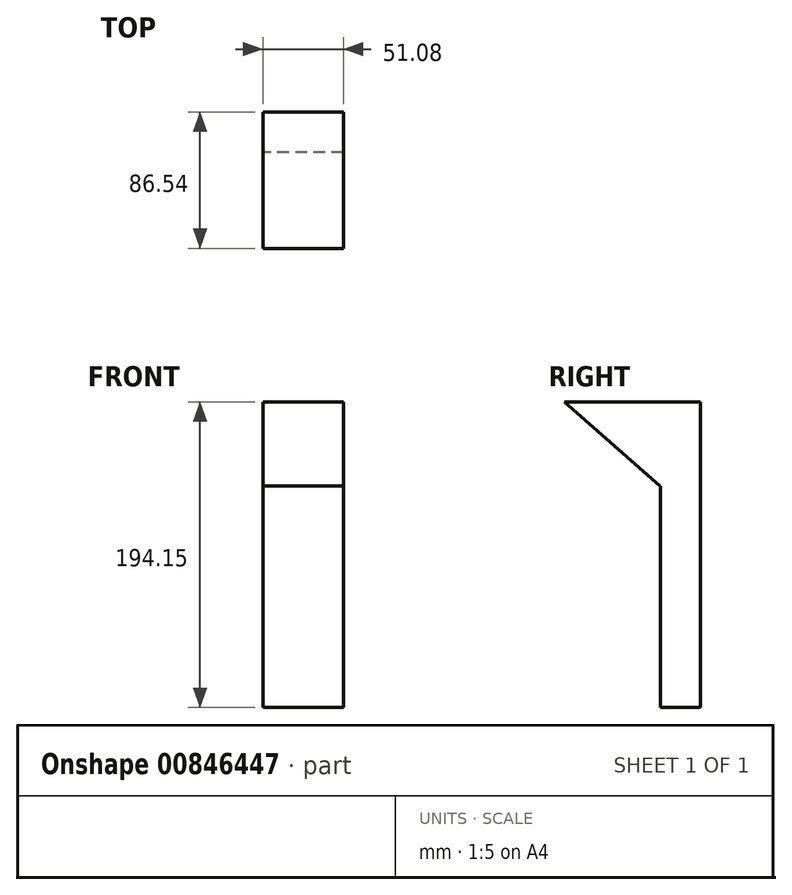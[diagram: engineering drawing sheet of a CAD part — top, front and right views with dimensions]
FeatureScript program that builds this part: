
annotation { "Feature Type Name" : "Feature", "Feature Type Description" : "" }
export const myFeature = defineFeature(function(context is Context, id is Id, definition is map)
    precondition{}
    {
        {
            var Q0;
            Q0=qCreatedBy(makeId("Front.planeOp"),FACE);
            var sketch = newSketch(context, id + "F0", { "sketchPlane" : qUnion([Q0])});
            skLineSegment(sketch, "E0.bottom", {"start": v(-51.08, -57.08) * mm, "end": v(0, -57.08) * mm});
            skLineSegment(sketch, "E0.top", {"start": v(-51.08, 60.33) * mm, "end": v(0, 60.33) * mm});
            skLineSegment(sketch, "E0.left", {"start": v(-51.08, -57.08) * mm, "end": v(-51.08, 60.33) * mm});
            skLineSegment(sketch, "E0.right", {"start": v(0, -57.08) * mm, "end": v(0, 60.33) * mm});
            skSolve(sketch);
        }
        {
            var Q0;
            Q0=makeQuery(id+"F0.imprint","IMPRINT",FACE,{"disambiguationData":[TD([[makeQuery(id+"F0.imprint","IMPRINT",EDGE,{"derivedFrom":sQuery(id+"F0.wireOp",EDGE,"E0.bottom")}),1.0]])]});
            extrude(context, id + "F1", {"entities" : qUnion([Q0]), "depth" : 25.4 * mm, "offsetDistance" : 25.4 * mm});
        }
        {
            var Q0;
            Q0=makeQuery(id+"F1.opExtrude","SWEPT_FACE",FACE,{"disambiguationData":[OSD([sQuery(id+"F0.wireOp",EDGE,"E0.top")])]});
            extrude(context, id + "F2", {"entities" : qUnion([Q0]), "operationType" : NewBodyOperationType.ADD, "depth" : 76.74 * mm, "offsetDistance" : 25.4 * mm});
        }
        {
            var Q0;
            {var subQ0=sQuery(id+"F0.wireOp",EDGE,"E0.top");Q0=makeQuery(id+"F2.boolean.opBoolean","MERGE",FACE,{"derivedFrom":[makeQuery(id+"F1.opExtrude","CAP_FACE",FACE,{"disambiguationData":[OSD([sQuery(id+"F0.wireOp",EDGE,"E0.bottom"),subQ0,sQuery(id+"F0.wireOp",EDGE,"E0.left"),sQuery(id+"F0.wireOp",EDGE,"E0.right")])],"isStart":false}),makeQuery(id+"F2.opExtrude","SWEPT_FACE",FACE,{"disambiguationData":[OSD([subQ0]),TDD([makeQuery(id+"F1.opExtrude","CAP_EDGE",EDGE,{"disambiguationData":[OSD([subQ0])],"isStart":false})])]})]});}
            var sketch = newSketch(context, id + "F3", { "sketchPlane" : qUnion([Q0])});
            skLineSegment(sketch, "E1", {"start": v(0, 83.74) * mm, "end": v(-51.08, 83.74) * mm});
            skSolve(sketch);
        }
        {
            var Q0;
            {var subQ0=sQuery(id+"F3.wireOp",EDGE,"E1");Q0=makeQuery(id+"F3.imprint","IMPRINT",FACE,{"disambiguationData":[TD([[makeQuery(id+"F3.imprint","IMPRINT",EDGE,{"derivedFrom":subQ0}),-1.0]])]});}
            extrude(context, id + "F4", {"entities" : qUnion([Q0]), "operationType" : NewBodyOperationType.ADD, "depth" : 61.16 * mm, "offsetDistance" : 25.4 * mm});
        }
        {
            var Q0;
            Q0=makeQuery(id+"F4.opExtrude","CAP_EDGE",EDGE,{"disambiguationData":[OSD([sQuery(id+"F3.wireOp",EDGE,"E1")])],"isStart":false});
            chamfer(context, id + "F5", {"entities" : qUnion([Q0]), "chamferType" : ChamferType.TWO_OFFSETS, "width1" : 60.96 * mm, "oppositeDirection" : false, "width2" : 53.34 * mm, "tangentPropagation" : true});
        }
    });
